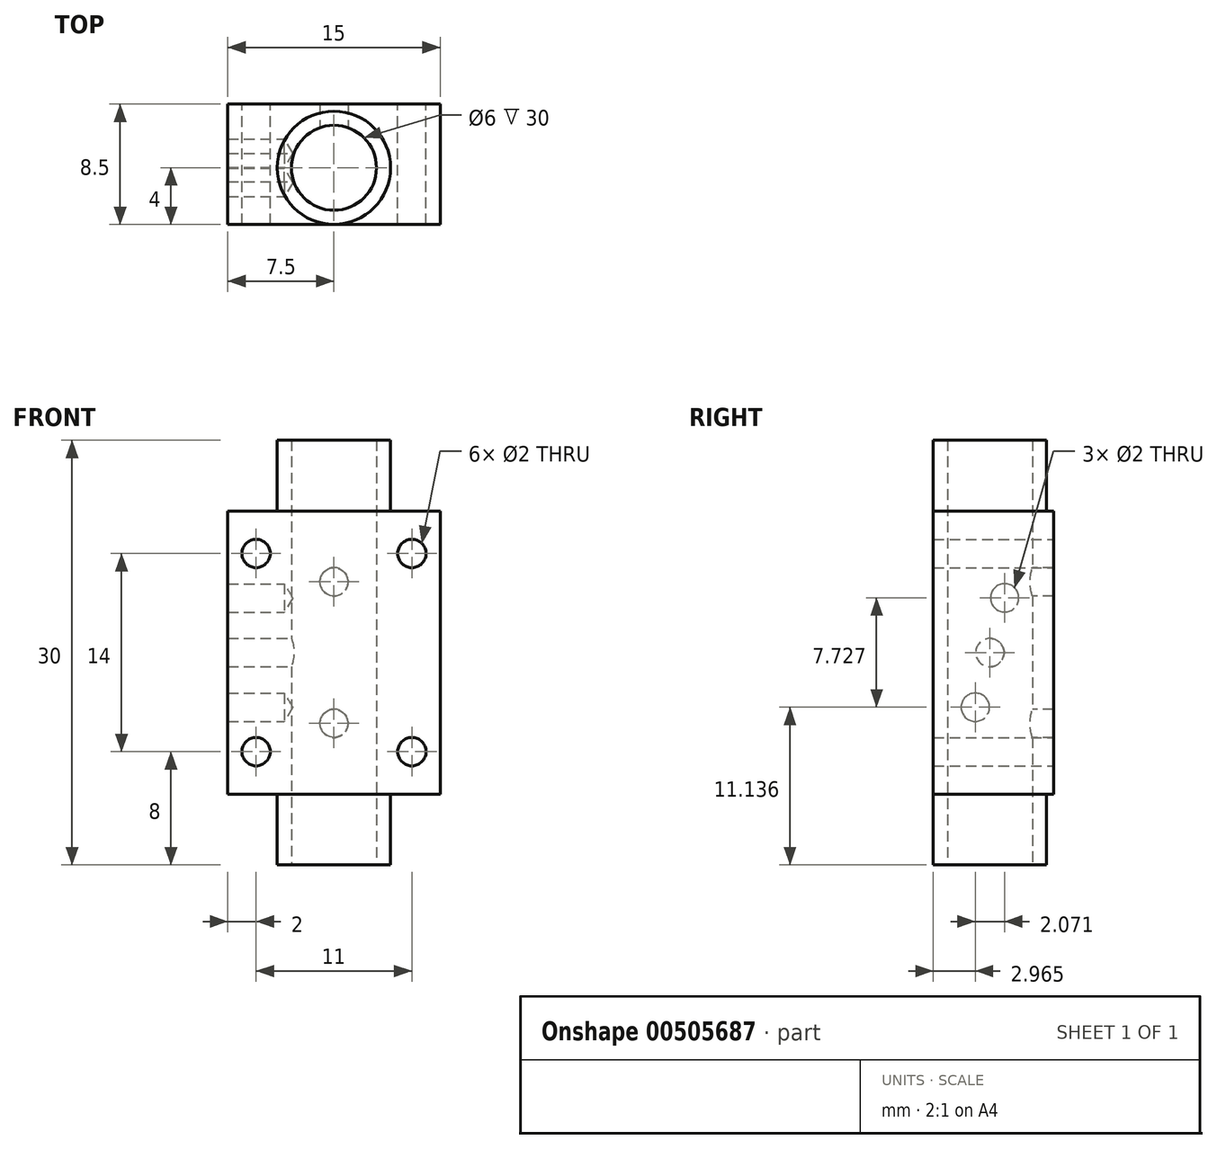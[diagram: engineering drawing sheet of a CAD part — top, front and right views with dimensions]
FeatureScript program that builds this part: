
annotation { "Feature Type Name" : "Feature", "Feature Type Description" : "" }
export const myFeature = defineFeature(function(context is Context, id is Id, definition is map)
    precondition{}
    {
        {
            var Q0;
            Q0=qCreatedBy(makeId("Front.planeOp"),FACE);
            var sketch = newSketch(context, id + "F0", { "sketchPlane" : qUnion([Q0])});
            skLineSegment(sketch, "E0.bottom", {"start": v(-7.5, 10) * mm, "end": v(7.5, 10) * mm});
            skLineSegment(sketch, "E0.top", {"start": v(-7.5, -10) * mm, "end": v(7.5, -10) * mm});
            skLineSegment(sketch, "E0.left", {"start": v(-7.5, 10) * mm, "end": v(-7.5, -10) * mm});
            skLineSegment(sketch, "E0.right", {"start": v(7.5, 10) * mm, "end": v(7.5, -10) * mm});
            skLineSegment(sketch, "E1.top", {"start": v(-4, 10) * mm, "end": v(4, 10) * mm});
            skLineSegment(sketch, "E2.bottom", {"start": v(-4, -10) * mm, "end": v(4, -10) * mm});
            skPoint(sketch, "E3", {"position": v(0, -10) * mm});
            skPoint(sketch, "E4", {"position": v(0, 10) * mm});
            skLineSegment(sketch, "E5", {"start": v(0, 10) * mm, "end": v(0, -10) * mm, "construction": true});
            skLineSegment(sketch, "E6", {"start": v(-7.5, 0) * mm, "end": v(7.5, 0) * mm, "construction": true});
            skLineSegment(sketch, "E7", {"start": v(-6.5, 7) * mm, "end": v(6.57, 7) * mm, "construction": true});
            skLineSegment(sketch, "E8", {"start": v(-6.3, -7) * mm, "end": v(6.36, -7) * mm, "construction": true});
            skLineSegment(sketch, "E9", {"start": v(-5.5, 7) * mm, "end": v(-5.5, -7) * mm, "construction": true});
            skLineSegment(sketch, "E10", {"start": v(5.5, 7) * mm, "end": v(5.5, -7) * mm, "construction": true});
            skCircle(sketch, "E11", {"center": v(-5.5, 7) * mm, "radius": 1 * mm});
            skCircle(sketch, "E12", {"center": v(5.5, 7) * mm, "radius": 1 * mm});
            skCircle(sketch, "E13", {"center": v(-5.5, -7) * mm, "radius": 1 * mm});
            skCircle(sketch, "E14", {"center": v(5.5, -7) * mm, "radius": 1 * mm});
            skPoint(sketch, "E15", {"position": v(0, -5) * mm});
            skPoint(sketch, "E16", {"position": v(0, 5) * mm});
            skCircle(sketch, "E17", {"center": v(0, 5) * mm, "radius": 0.9 * mm, "construction": true});
            skCircle(sketch, "E18", {"center": v(0, -5) * mm, "radius": 0.9 * mm, "construction": true});
            skSolve(sketch);
        }
        {
            var Q0;
            {var subQ3=sQuery(id+"F0.wireOp",EDGE,"E0.left");Q0=makeQuery(id+"F0.imprint","IMPRINT",FACE,{"disambiguationData":[TD([[makeQuery(id+"F0.imprint","IMPRINT",EDGE,{"derivedFrom":subQ3}),1.0]])]});}
            var Q1;
            Q1 = qSketchRegion(id + "F2", true);
            extrude(context, id + "F1", {"entities" : qUnion([Q0, Q1]), "depth" : 8.5 * mm});
        }
        {
            var Q0;
            Q0=makeQuery(id+"F1.opExtrude","SWEPT_FACE",FACE,{"disambiguationData":[OSD([sQuery(id+"F0.wireOp",EDGE,"E0.bottom"),sQuery(id+"F0.wireOp",EDGE,"E1.top")])]});
            var sketch = newSketch(context, id + "F2", { "sketchPlane" : qUnion([Q0])});
            skLineSegment(sketch, "E19", {"start": v(-7.5, -4.5) * mm, "end": v(7.5, -4.5) * mm, "construction": true});
            skPoint(sketch, "E20", {"position": v(0, -4.5) * mm});
            skCircle(sketch, "E21", {"center": v(0, -4.5) * mm, "radius": 4 * mm});
            skCircle(sketch, "E22", {"center": v(0, -4.5) * mm, "radius": 3 * mm});
            skLineSegment(sketch, "E23", {"start": v(0, 0) * mm, "end": v(0, -11.3) * mm, "construction": true});
            skSolve(sketch);
        }
        {
            var Q0;
            Q0=sQuery(id+"F2.wireOp",VERTEX,"E20");
            var Q1;
            Q1=makeQuery(id+"F1.opExtrude","SWEPT_BODY",BODY,{"disambiguationData":[OSD([sQuery(id+"F0.wireOp",EDGE,"E0.bottom"),sQuery(id+"F0.wireOp",EDGE,"E0.top"),sQuery(id+"F0.wireOp",EDGE,"E0.left"),sQuery(id+"F0.wireOp",EDGE,"E0.right"),sQuery(id+"F0.wireOp",EDGE,"E1.top"),sQuery(id+"F0.wireOp",EDGE,"E2.bottom"),sQuery(id+"F0.wireOp",EDGE,"E11"),sQuery(id+"F0.wireOp",EDGE,"E12"),sQuery(id+"F0.wireOp",EDGE,"E13"),sQuery(id+"F0.wireOp",EDGE,"E14")])]});
            hole(context, id + "F3", {"style" : HoleStyle.SIMPLE, "endStyle" : HoleEndStyle.BLIND, "holeDiameter" : 6 * mm, "holeDepth" : 30 * mm, "isTappedThrough" : true, "tappedDepth" : 12 * mm, "tapClearance" : 3, "locations" : qUnion([Q0]), "scope" : qUnion([Q1]), "startStyle" : HoleStartStyle.PART});
        }
        {
            var Q0;
            Q0=makeQuery(id+"F2.imprint","IMPRINT",FACE,{"disambiguationData":[TD([[makeQuery(id+"F2.imprint","IMPRINT",EDGE,{"derivedFrom":sQuery(id+"F2.wireOp",EDGE,"E21")}),1.0]])]});
            extrude(context, id + "F4", {"entities" : qUnion([Q0]), "operationType" : NewBodyOperationType.ADD, "depth" : 5 * mm});
        }
        {
            var Q0;
            Q0=makeQuery(id+"F1.opExtrude","SWEPT_FACE",FACE,{"disambiguationData":[OSD([sQuery(id+"F0.wireOp",EDGE,"E0.top"),sQuery(id+"F0.wireOp",EDGE,"E2.bottom")])]});
            var sketch = newSketch(context, id + "F5", { "sketchPlane" : qUnion([Q0])});
            skCircle(sketch, "E24", {"center": v(0, 4.5) * mm, "radius": 4 * mm});
            skSolve(sketch);
        }
        {
            var Q0;
            Q0=makeQuery(id+"F5.imprint","IMPRINT",FACE,{"disambiguationData":[TD([[makeQuery(id+"F5.imprint","IMPRINT",EDGE,{"derivedFrom":sQuery(id+"F5.wireOp",EDGE,"E24")}),1.0]])]});
            var Q1;
            Q1 = qSketchRegion(id + "F7", true);
            extrude(context, id + "F6", {"entities" : qUnion([Q0, Q1]), "operationType" : NewBodyOperationType.ADD, "depth" : 5 * mm});
        }
        {
            var Q0;
            Q0=makeQuery(id+"F1.opExtrude","SWEPT_FACE",FACE,{"disambiguationData":[OSD([sQuery(id+"F0.wireOp",EDGE,"E0.left")])]});
            var sketch = newSketch(context, id + "F7", { "sketchPlane" : qUnion([Q0])});
            skLineSegment(sketch, "E25", {"start": v(4.5, 10) * mm, "end": v(4.5, -11.13) * mm, "construction": true});
            skPoint(sketch, "E25.endSnap0", {"position": v(4.5, -10) * mm});
            skLineSegment(sketch, "E26", {"start": v(0, 16.8) * mm, "end": v(9.04, -16.94) * mm, "construction": true});
            skLineSegment(sketch, "E27", {"start": v(0, 0) * mm, "end": v(8.5, 0) * mm, "construction": true});
            skPoint(sketch, "E28", {"position": v(4.5, 0) * mm});
            skPoint(sketch, "E29", {"position": v(3.46, 3.86) * mm});
            skPoint(sketch, "E30", {"position": v(5.54, -3.86) * mm});
            skCircle(sketch, "E31", {"center": v(3.46, 3.86) * mm, "radius": 1 * mm});
            skCircle(sketch, "E32", {"center": v(4.5, 0) * mm, "radius": 1 * mm});
            skCircle(sketch, "E33", {"center": v(5.54, -3.86) * mm, "radius": 1 * mm});
            skSolve(sketch);
        }
        {
            var Q0;
            Q0=sQuery(id+"F7.wireOp",VERTEX,"E28");
            var Q1;
            Q1=makeQuery(id+"F1.opExtrude","SWEPT_BODY",BODY,{"disambiguationData":[OSD([sQuery(id+"F0.wireOp",EDGE,"E0.bottom"),sQuery(id+"F0.wireOp",EDGE,"E0.top"),sQuery(id+"F0.wireOp",EDGE,"E0.left"),sQuery(id+"F0.wireOp",EDGE,"E0.right"),sQuery(id+"F0.wireOp",EDGE,"E1.top"),sQuery(id+"F0.wireOp",EDGE,"E2.bottom"),sQuery(id+"F0.wireOp",EDGE,"E11"),sQuery(id+"F0.wireOp",EDGE,"E12"),sQuery(id+"F0.wireOp",EDGE,"E13"),sQuery(id+"F0.wireOp",EDGE,"E14")])]});
            hole(context, id + "F8", {"style" : HoleStyle.SIMPLE, "endStyle" : HoleEndStyle.BLIND, "holeDiameter" : 2 * mm, "holeDepth" : 7 * mm, "isTappedThrough" : true, "tappedDepth" : 12 * mm, "tapClearance" : 3, "locations" : qUnion([Q0]), "scope" : qUnion([Q1]), "startStyle" : HoleStartStyle.PART});
        }
        {
            var Q0;
            Q0=makeQuery(id+"F1.opExtrude","CAP_FACE",FACE,{"disambiguationData":[OSD([sQuery(id+"F0.wireOp",EDGE,"E0.bottom"),sQuery(id+"F0.wireOp",EDGE,"E0.top"),sQuery(id+"F0.wireOp",EDGE,"E0.left"),sQuery(id+"F0.wireOp",EDGE,"E0.right"),sQuery(id+"F0.wireOp",EDGE,"E1.top"),sQuery(id+"F0.wireOp",EDGE,"E2.bottom"),sQuery(id+"F0.wireOp",EDGE,"E11"),sQuery(id+"F0.wireOp",EDGE,"E12"),sQuery(id+"F0.wireOp",EDGE,"E13"),sQuery(id+"F0.wireOp",EDGE,"E14")])],"isStart":false});
            var sketch = newSketch(context, id + "F9", { "sketchPlane" : qUnion([Q0])});
            skLineSegment(sketch, "E34", {"start": v(0, 10) * mm, "end": v(0, -10) * mm, "construction": true});
            skLineSegment(sketch, "E35", {"start": v(-1.34, -5) * mm, "end": v(1.76, -5) * mm, "construction": true});
            skLineSegment(sketch, "E36", {"start": v(-1.57, 5) * mm, "end": v(1.82, 5) * mm, "construction": true});
            skPoint(sketch, "E37", {"position": v(0, 5) * mm});
            skPoint(sketch, "E38", {"position": v(0, -5) * mm});
            skCircle(sketch, "E39", {"center": v(0, 5) * mm, "radius": 0.9 * mm});
            skCircle(sketch, "E40", {"center": v(0, -5) * mm, "radius": 0.9 * mm});
            skSolve(sketch);
        }
        {
            var Q0;
            Q0=makeQuery(id+"F1.opExtrude","SWEPT_FACE",FACE,{"disambiguationData":[OSD([sQuery(id+"F0.wireOp",EDGE,"E0.left")])]});
            var sketch = newSketch(context, id + "F10", { "sketchPlane" : qUnion([Q0])});
            skLineSegment(sketch, "E41", {"start": v(4.5, 14.27) * mm, "end": v(4.5, -14.13) * mm, "construction": true});
            skLineSegment(sketch, "E42", {"start": v(0, 0) * mm, "end": v(8.5, 0) * mm, "construction": true});
            skPoint(sketch, "E43", {"position": v(4.5, 0) * mm});
            skLineSegment(sketch, "E44", {"start": v(5.84, -5) * mm, "end": v(2.34, 8.05) * mm, "construction": true});
            skPoint(sketch, "E45", {"position": v(5.54, -3.86) * mm});
            skPoint(sketch, "E46", {"position": v(3.46, 3.86) * mm});
            skCircle(sketch, "E47", {"center": v(5.54, -3.86) * mm, "radius": 1 * mm});
            skCircle(sketch, "E48", {"center": v(3.46, 3.86) * mm, "radius": 1 * mm});
            skSolve(sketch);
        }
        {
            var Q0;
            Q0=sQuery(id+"F10.wireOp",VERTEX,"E47.center");
            var Q1;
            Q1=sQuery(id+"F10.wireOp",VERTEX,"E46");
            var Q2;
            Q2=makeQuery(id+"F1.opExtrude","SWEPT_BODY",BODY,{"disambiguationData":[OSD([sQuery(id+"F0.wireOp",EDGE,"E0.bottom"),sQuery(id+"F0.wireOp",EDGE,"E0.top"),sQuery(id+"F0.wireOp",EDGE,"E0.left"),sQuery(id+"F0.wireOp",EDGE,"E0.right"),sQuery(id+"F0.wireOp",EDGE,"E1.top"),sQuery(id+"F0.wireOp",EDGE,"E2.bottom"),sQuery(id+"F0.wireOp",EDGE,"E11"),sQuery(id+"F0.wireOp",EDGE,"E12"),sQuery(id+"F0.wireOp",EDGE,"E13"),sQuery(id+"F0.wireOp",EDGE,"E14")])]});
            hole(context, id + "F11", {"style" : HoleStyle.SIMPLE, "endStyle" : HoleEndStyle.BLIND, "holeDiameter" : 2 * mm, "holeDepth" : 4 * mm, "isTappedThrough" : true, "tappedDepth" : 12 * mm, "tapClearance" : 3, "locations" : qUnion([Q0, Q1]), "scope" : qUnion([Q2]), "startStyle" : HoleStartStyle.PART});
        }
        {
            var Q0;
            Q0=makeQuery(id+"F1.opExtrude","CAP_FACE",FACE,{"disambiguationData":[OSD([sQuery(id+"F0.wireOp",EDGE,"E0.bottom"),sQuery(id+"F0.wireOp",EDGE,"E0.top"),sQuery(id+"F0.wireOp",EDGE,"E0.left"),sQuery(id+"F0.wireOp",EDGE,"E0.right"),sQuery(id+"F0.wireOp",EDGE,"E1.top"),sQuery(id+"F0.wireOp",EDGE,"E2.bottom"),sQuery(id+"F0.wireOp",EDGE,"E11"),sQuery(id+"F0.wireOp",EDGE,"E12"),sQuery(id+"F0.wireOp",EDGE,"E13"),sQuery(id+"F0.wireOp",EDGE,"E14")])],"isStart":true});
            var sketch = newSketch(context, id + "F12", { "sketchPlane" : qUnion([Q0])});
            skLineSegment(sketch, "E49", {"start": v(0, 10) * mm, "end": v(0, -10) * mm, "construction": true});
            skLineSegment(sketch, "E50", {"start": v(-1.6, -5) * mm, "end": v(1.42, -5) * mm, "construction": true});
            skLineSegment(sketch, "E51", {"start": v(-1.68, 5) * mm, "end": v(1.63, 5) * mm, "construction": true});
            skCircle(sketch, "E52", {"center": v(0, 5) * mm, "radius": 0.9 * mm});
            skCircle(sketch, "E53", {"center": v(0, -5) * mm, "radius": 0.9 * mm});
            skSolve(sketch);
        }
        {
            var Q0;
            Q0=sQuery(id+"F12.wireOp",VERTEX,"E52.center");
            var Q1;
            Q1=sQuery(id+"F12.wireOp",VERTEX,"E53.center");
            var Q2;
            Q2=makeQuery(id+"F1.opExtrude","SWEPT_BODY",BODY,{"disambiguationData":[OSD([sQuery(id+"F0.wireOp",EDGE,"E0.bottom"),sQuery(id+"F0.wireOp",EDGE,"E0.top"),sQuery(id+"F0.wireOp",EDGE,"E0.left"),sQuery(id+"F0.wireOp",EDGE,"E0.right"),sQuery(id+"F0.wireOp",EDGE,"E1.top"),sQuery(id+"F0.wireOp",EDGE,"E2.bottom"),sQuery(id+"F0.wireOp",EDGE,"E11"),sQuery(id+"F0.wireOp",EDGE,"E12"),sQuery(id+"F0.wireOp",EDGE,"E13"),sQuery(id+"F0.wireOp",EDGE,"E14")])]});
            hole(context, id + "F13", {"style" : HoleStyle.SIMPLE, "endStyle" : HoleEndStyle.BLIND, "holeDiameter" : 2 * mm, "holeDepth" : 4 * mm, "isTappedThrough" : true, "tappedDepth" : 12 * mm, "tapClearance" : 3, "locations" : qUnion([Q0, Q1]), "scope" : qUnion([Q2]), "startStyle" : HoleStartStyle.PART});
        }
    });
